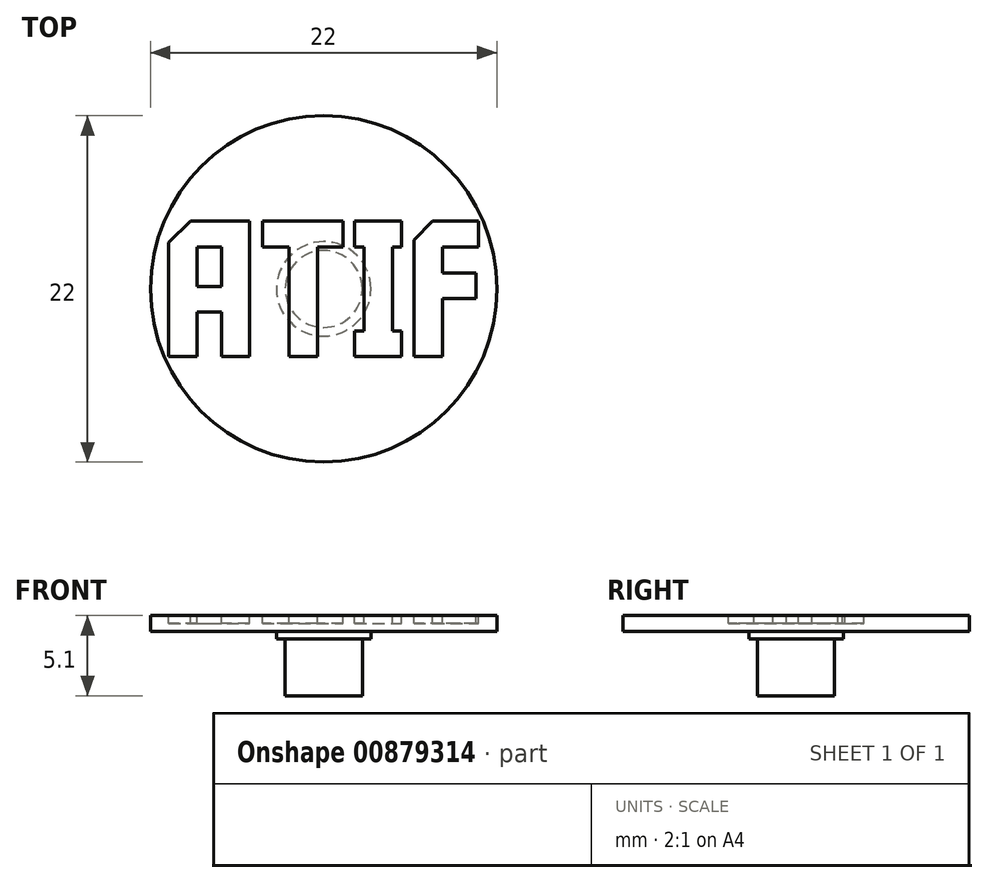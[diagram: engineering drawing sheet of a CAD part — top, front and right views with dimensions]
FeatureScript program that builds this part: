
annotation { "Feature Type Name" : "Feature", "Feature Type Description" : "" }
export const myFeature = defineFeature(function(context is Context, id is Id, definition is map)
    precondition{}
    {
        {
            var Q0;
            Q0=qCreatedBy(makeId("Top.planeOp"),FACE);
            var sketch = newSketch(context, id + "F0", { "sketchPlane" : qUnion([Q0])});
            skCircle(sketch, "E0", {"center": v(0, 0) * mm, "radius": 2.45 * mm});
            skSolve(sketch);
        }
        {
            var Q0;
            Q0=makeQuery(id+"F0.imprint","IMPRINT",FACE,{"disambiguationData":[TD([[makeQuery(id+"F0.imprint","IMPRINT",EDGE,{"derivedFrom":sQuery(id+"F0.wireOp",EDGE,"E0")}),1.0]])]});
            extrude(context, id + "F1", {"entities" : qUnion([Q0]), "depth" : 3.6 * mm, "offsetDistance" : 25.4 * mm});
        }
        {
            var Q0;
            Q0=makeQuery(id+"F1.opExtrude","CAP_FACE",FACE,{"disambiguationData":[OSD([sQuery(id+"F0.wireOp",EDGE,"E0")])],"isStart":false});
            var sketch = newSketch(context, id + "F2", { "sketchPlane" : qUnion([Q0])});
            skCircle(sketch, "E1", {"center": v(0, 0) * mm, "radius": 3 * mm});
            skSolve(sketch);
        }
        {
            var Q0;
            Q0=makeQuery(id+"F2.imprint","IMPRINT",FACE,{"disambiguationData":[TD([[makeQuery(id+"F2.imprint","IMPRINT",EDGE,{"derivedFrom":sQuery(id+"F2.wireOp",EDGE,"E1")}),1.0]])]});
            var Q1;
            Q1=makeQuery(id+"F2.imprint","IMPRINT",FACE,{"disambiguationData":[TD([[makeQuery(id+"F2.imprint","IMPRINT",EDGE,{"derivedFrom":makeQuery(id+"F1.opExtrude","CAP_EDGE",EDGE,{"disambiguationData":[OSD([sQuery(id+"F0.wireOp",EDGE,"E0")])],"isStart":false})}),1.0]])]});
            extrude(context, id + "F3", {"entities" : qUnion([Q0, Q1]), "operationType" : NewBodyOperationType.ADD, "depth" : 0.5 * mm, "offsetDistance" : 25.4 * mm});
        }
        {
            var Q0;
            Q0=makeQuery(id+"F3.opExtrude","CAP_FACE",FACE,{"disambiguationData":[OSD([sQuery(id+"F2.wireOp",EDGE,"E1")])],"isStart":false});
            var sketch = newSketch(context, id + "F4", { "sketchPlane" : qUnion([Q0])});
            skCircle(sketch, "E2", {"center": v(0, 0) * mm, "radius": 11 * mm});
            skSolve(sketch);
        }
        {
            var Q0;
            Q0=makeQuery(id+"F4.imprint","IMPRINT",FACE,{"disambiguationData":[TD([[makeQuery(id+"F4.imprint","IMPRINT",EDGE,{"derivedFrom":sQuery(id+"F4.wireOp",EDGE,"E2")}),1.0]])]});
            var Q1;
            Q1=makeQuery(id+"F4.imprint","IMPRINT",FACE,{"disambiguationData":[TD([[makeQuery(id+"F4.imprint","IMPRINT",EDGE,{"derivedFrom":makeQuery(id+"F3.opExtrude","CAP_EDGE",EDGE,{"disambiguationData":[OSD([sQuery(id+"F2.wireOp",EDGE,"E1")])],"isStart":false})}),1.0]])]});
            extrude(context, id + "F5", {"entities" : qUnion([Q0, Q1]), "operationType" : NewBodyOperationType.ADD, "depth" : 1 * mm, "offsetDistance" : 25.4 * mm});
        }
        {
            var Q0;
            Q0=makeQuery(id+"F5.opExtrude","CAP_FACE",FACE,{"disambiguationData":[OSD([sQuery(id+"F4.wireOp",EDGE,"E2")])],"isStart":false});
            var sketch = newSketch(context, id + "F6", { "sketchPlane" : qUnion([Q0])});
            skLineSegment(sketch, "E3", {"start": v(-8.03, -4.3) * mm, "end": v(-9.84, -4.3) * mm});
            skLineSegment(sketch, "E4", {"start": v(-9.84, -4.3) * mm, "end": v(-9.84, 2.94) * mm});
            skLineSegment(sketch, "E5", {"start": v(-9.84, 2.94) * mm, "end": v(-8.45, 4.3) * mm});
            skLineSegment(sketch, "E6", {"start": v(-8.45, 4.3) * mm, "end": v(-4.7, 4.3) * mm});
            skLineSegment(sketch, "E7", {"start": v(-4.7, 4.3) * mm, "end": v(-4.7, -4.3) * mm});
            skLineSegment(sketch, "E8", {"start": v(-4.7, -4.3) * mm, "end": v(-6.5, -4.3) * mm});
            skLineSegment(sketch, "E9", {"start": v(-6.5, -4.3) * mm, "end": v(-6.5, -1.48) * mm});
            skLineSegment(sketch, "E10", {"start": v(-6.5, -1.48) * mm, "end": v(-8.03, -1.48) * mm});
            skLineSegment(sketch, "E11", {"start": v(-8.03, -1.48) * mm, "end": v(-8.03, -4.3) * mm});
            skLineSegment(sketch, "E12", {"start": v(-6.5, 0.16) * mm, "end": v(-6.5, 2.67) * mm});
            skLineSegment(sketch, "E13", {"start": v(-6.5, 2.67) * mm, "end": v(-8.03, 2.67) * mm});
            skLineSegment(sketch, "E14", {"start": v(-8.03, 2.67) * mm, "end": v(-8.03, 0.16) * mm});
            skLineSegment(sketch, "E15", {"start": v(-8.03, 0.16) * mm, "end": v(-6.5, 0.16) * mm});
            skLineSegment(sketch, "E16", {"start": v(1.23, 2.67) * mm, "end": v(-0.4, 2.67) * mm});
            skLineSegment(sketch, "E17", {"start": v(-0.4, 2.67) * mm, "end": v(-0.4, -4.3) * mm});
            skLineSegment(sketch, "E18", {"start": v(-0.4, -4.3) * mm, "end": v(-2.2, -4.3) * mm});
            skLineSegment(sketch, "E19", {"start": v(-2.2, -4.3) * mm, "end": v(-2.2, 2.67) * mm});
            skLineSegment(sketch, "E20", {"start": v(-2.2, 2.67) * mm, "end": v(-3.9, 2.67) * mm});
            skLineSegment(sketch, "E21", {"start": v(-3.9, 2.67) * mm, "end": v(-3.9, 4.3) * mm});
            skLineSegment(sketch, "E22", {"start": v(-3.9, 4.3) * mm, "end": v(1.23, 4.3) * mm});
            skLineSegment(sketch, "E23", {"start": v(1.23, 4.3) * mm, "end": v(1.23, 2.67) * mm});
            skLineSegment(sketch, "E24", {"start": v(4.96, -2.67) * mm, "end": v(4.96, -4.3) * mm});
            skLineSegment(sketch, "E25", {"start": v(4.96, -4.3) * mm, "end": v(1.96, -4.3) * mm});
            skLineSegment(sketch, "E26", {"start": v(1.96, -4.3) * mm, "end": v(1.96, -2.67) * mm});
            skLineSegment(sketch, "E27", {"start": v(1.96, -2.67) * mm, "end": v(2.56, -2.67) * mm});
            skLineSegment(sketch, "E28", {"start": v(2.56, -2.67) * mm, "end": v(2.56, 2.67) * mm});
            skLineSegment(sketch, "E29", {"start": v(2.56, 2.67) * mm, "end": v(1.96, 2.67) * mm});
            skLineSegment(sketch, "E30", {"start": v(1.96, 2.67) * mm, "end": v(1.96, 4.3) * mm});
            skLineSegment(sketch, "E31", {"start": v(1.96, 4.3) * mm, "end": v(4.96, 4.3) * mm});
            skLineSegment(sketch, "E32", {"start": v(4.96, 4.3) * mm, "end": v(4.96, 2.67) * mm});
            skLineSegment(sketch, "E33", {"start": v(4.96, 2.67) * mm, "end": v(4.36, 2.67) * mm});
            skLineSegment(sketch, "E34", {"start": v(4.36, 2.67) * mm, "end": v(4.36, -2.67) * mm});
            skLineSegment(sketch, "E35", {"start": v(4.36, -2.67) * mm, "end": v(4.96, -2.67) * mm});
            skLineSegment(sketch, "E36", {"start": v(7.53, -0.6) * mm, "end": v(7.53, -4.3) * mm});
            skLineSegment(sketch, "E37", {"start": v(7.53, -4.3) * mm, "end": v(5.73, -4.3) * mm});
            skLineSegment(sketch, "E38", {"start": v(5.73, -4.3) * mm, "end": v(5.73, 3.11) * mm});
            skLineSegment(sketch, "E39", {"start": v(5.73, 3.11) * mm, "end": v(6.92, 4.3) * mm});
            skLineSegment(sketch, "E40", {"start": v(6.92, 4.3) * mm, "end": v(9.84, 4.3) * mm});
            skLineSegment(sketch, "E41", {"start": v(9.84, 4.3) * mm, "end": v(9.84, 2.67) * mm});
            skLineSegment(sketch, "E42", {"start": v(9.84, 2.67) * mm, "end": v(7.53, 2.67) * mm});
            skLineSegment(sketch, "E43", {"start": v(7.53, 2.67) * mm, "end": v(7.53, 1) * mm});
            skLineSegment(sketch, "E44", {"start": v(7.53, 1) * mm, "end": v(9.66, 1) * mm});
            skLineSegment(sketch, "E45", {"start": v(9.66, 1) * mm, "end": v(9.66, -0.6) * mm});
            skLineSegment(sketch, "E46", {"start": v(9.66, -0.6) * mm, "end": v(7.53, -0.6) * mm});
            skSolve(sketch);
        }
        {
            var Q0;
            Q0 = qSketchRegion(id + "F6", true);
            extrude(context, id + "F7", {"entities" : qUnion([Q0]), "operationType" : NewBodyOperationType.REMOVE, "oppositeDirection" : true, "depth" : 0.5 * mm, "offsetDistance" : 25.4 * mm});
        }
    });
